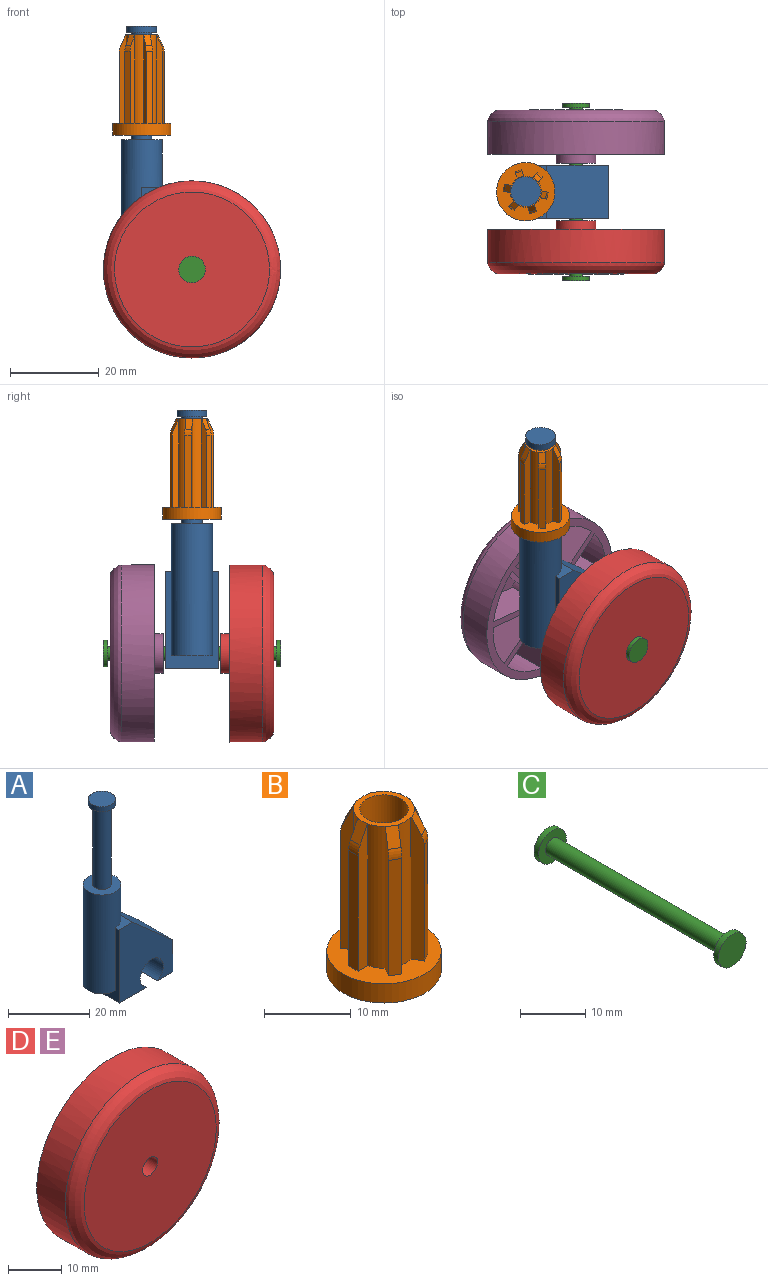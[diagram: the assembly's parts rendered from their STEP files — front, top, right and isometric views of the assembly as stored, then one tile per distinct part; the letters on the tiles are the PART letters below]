
ASSEMBLY  parts=5 mates=5
PART A: 16 faces, bbox 23.4x12x58.5 mm
  f0: plane 12x9.41mm, normal (0,0,-1), area 113mm2, adj f2,f5,f9,f10
  f1: plane 12x5.41mm, normal (0,0,-1), area 65mm2, adj f2,f8,f9,f10
  f2: plane 22x18.7mm, normal (0,-1,0), area 276.2mm2, adj f0,f1,f5,f6,f7,f8,f10
  f3: cylinder r=4.65mm len=29.8mm, axis (0,0,-1), area 593.1mm2, adj f4,f5,f7,f11
  f4: plane 9.3x4.65mm, normal (0,0,-1), area 34mm2, adj f3,f5
  f5: plane 22x12mm, normal (-1,0,0), area 87.3mm2, adj f0,f2,f3,f4,f7,f9
  f6: plane 14x12.32mm, normal (0.66,0,0.75), area 223.8mm2, adj f2,f7,f8,f9
  f7: plane 12x4.7mm, normal (0,0,1), area 22.4mm2, adj f2,f3,f5,f6,f9
  f8: plane 12x9.68mm, normal (1,0,0), area 116.1mm2, adj f1,f2,f6,f9
  f9: plane 22x18.7mm, normal (0,1,0), area 276.2mm2, adj f0,f1,f5,f6,f7,f8,f10
  f10: cylinder r=4mm len=12mm, axis (0,-1,0), area 253.1mm2, adj f0,f1,f2,f9
  f11: plane 9.3x9.3mm, normal (0,0,1), area 51.3mm2, adj f3,f15
  f12: plane 6.7x6.7mm, normal (0,0,1), area 35.3mm2, adj f13
  f13: cylinder r=3.35mm len=6.7mm, axis (0,0,-1), area 31.6mm2, adj f12,f14
  f14: plane 6.7x6.7mm, normal (0,0,-1), area 18.6mm2, adj f13,f15
  f15: cylinder r=2.3mm len=24.2mm, axis (0,0,-1), area 349.7mm2, adj f11,f14
PART B: 41 faces, bbox 13.2x13.2x22.7 mm
  f0: plane 13.2x13.2mm, normal (0,0,1), area 84.1mm2, adj f1,f2,f3,f4,f5,f7,f9,f11
  f1: cylinder r=3.5mm len=20mm, axis (0,0,1), area 42mm2, adj f0,f8,f27,f32
  f2: cylinder r=3.5mm len=20mm, axis (0,0,1), area 42mm2, adj f0,f8,f23,f28
  f3: cylinder r=3.5mm len=20mm, axis (0,0,1), area 42mm2, adj f0,f8,f19,f24
  f4: cylinder r=3.5mm len=20mm, axis (0,0,1), area 42mm2, adj f0,f8,f15,f20
  f5: cylinder r=3.5mm len=20mm, axis (0,0,1), area 42mm2, adj f0,f8,f11,f16
  f6: cylinder r=2.8mm len=22.7mm, axis (0,0,1), area 399.4mm2, adj f8,f10
  f7: cylinder r=3.5mm len=20mm, axis (0,0,1), area 42mm2, adj f0,f8,f12,f31
  f8: plane 7x7mm, normal (0,0,1), area 14.1mm2, adj f1,f2,f3,f4,f5,f6,f7,f11
  f9: cylinder r=6.6mm len=13.2mm, axis (0,0,1), area 112mm2, adj f0,f10
  f10: plane 13.2x13.2mm, normal (0,0,-1), area 112.2mm2, adj f6,f9
  f11: plane 20x1.59mm, normal (0,-1,0), area 29.4mm2, adj f0,f5,f8,f13,f14,f40
  f12: plane 20x1.59mm, normal (0,1,0), area 29.4mm2, adj f0,f7,f8,f13,f14,f40
  f13: plane 2.37x1.55mm, normal (0.89,0,0.45), area 4.1mm2, adj f8,f11,f12,f40
  f14: plane 16.29x1.55mm, normal (1,0,0), area 25.3mm2, adj f0,f11,f12,f40
  f15: plane 20x1.37mm, normal (-0.87,-0.5,0), area 29.4mm2, adj f0,f4,f8,f17,f18,f39
  f16: plane 20x1.37mm, normal (0.87,0.5,0), area 29.4mm2, adj f0,f5,f8,f17,f18,f39
  f17: plane 2.37x1.93mm, normal (0.45,-0.77,0.45), area 4.1mm2, adj f8,f15,f16,f39
  f18: plane 16.29x1.34mm, normal (0.5,-0.87,0), area 25.3mm2, adj f0,f15,f16,f39
  f19: plane 20x1.37mm, normal (-0.87,0.5,0), area 29.4mm2, adj f0,f3,f8,f21,f22,f38
  f20: plane 20x1.37mm, normal (0.87,-0.5,0), area 29.4mm2, adj f0,f4,f8,f21,f22,f38
  f21: plane 2.37x1.93mm, normal (-0.45,-0.77,0.45), area 4.1mm2, adj f8,f19,f20,f38
  f22: plane 16.29x1.34mm, normal (-0.5,-0.87,0), area 25.3mm2, adj f0,f19,f20,f38
  f23: plane 20x1.59mm, normal (0,1,0), area 29.4mm2, adj f0,f2,f8,f25,f26,f37
  f24: plane 20x1.59mm, normal (0,-1,0), area 29.4mm2, adj f0,f3,f8,f25,f26,f37
  f25: plane 2.37x1.55mm, normal (-0.89,0,0.45), area 4.1mm2, adj f8,f23,f24,f37
  f26: plane 16.29x1.55mm, normal (-1,0,0), area 25.3mm2, adj f0,f23,f24,f37
  f27: plane 20x1.37mm, normal (0.87,0.5,0), area 29.4mm2, adj f0,f1,f8,f29,f30,f36
  f28: plane 20x1.37mm, normal (-0.87,-0.5,0), area 29.4mm2, adj f0,f2,f8,f29,f30,f36
  f29: plane 2.37x1.93mm, normal (-0.45,0.77,0.45), area 4.1mm2, adj f8,f27,f28,f36
  f30: plane 16.29x1.34mm, normal (-0.5,0.87,0), area 25.3mm2, adj f0,f27,f28,f36
  f31: plane 20x1.37mm, normal (0.87,-0.5,0), area 29.4mm2, adj f0,f7,f8,f33,f34,f35
  f32: plane 20x1.37mm, normal (-0.87,0.5,0), area 29.4mm2, adj f0,f1,f8,f33,f34,f35
  f33: plane 2.37x1.93mm, normal (0.45,0.77,0.45), area 4.1mm2, adj f8,f31,f32,f35
  f34: plane 16.29x1.34mm, normal (0.5,0.87,0), area 25.3mm2, adj f0,f31,f32,f35
  f35: cylinder r=3mm len=1.5mm, axis (-0.87,0.5,0), area 2.2mm2, adj f31,f32,f33,f34
  f36: cylinder r=3mm len=1.5mm, axis (-0.87,-0.5,0), area 2.2mm2, adj f27,f28,f29,f30
  f37: cylinder r=3mm len=1.55mm, axis (0,-1,0), area 2.2mm2, adj f23,f24,f25,f26
  f38: cylinder r=3mm len=1.5mm, axis (0.87,-0.5,0), area 2.2mm2, adj f19,f20,f21,f22
  f39: cylinder r=3mm len=1.5mm, axis (0.87,0.5,0), area 2.2mm2, adj f15,f16,f17,f18
  f40: cylinder r=3mm len=1.55mm, axis (0,1,0), area 2.2mm2, adj f11,f12,f13,f14
PART C: 7 faces, bbox 6x40x6 mm
  f0: cylinder r=1.5mm len=38mm, axis (0,1,0), area 358.1mm2, adj f3,f6
  f1: cylinder r=3mm len=6mm, axis (0,-1,0), area 18.8mm2, adj f2,f3
  f2: plane 6x6mm, normal (0,1,0), area 28.3mm2, adj f1
  f3: plane 6x6mm, normal (0,-1,0), area 21.2mm2, adj f0,f1
  f4: cylinder r=3mm len=6mm, axis (0,1,0), area 18.8mm2, adj f5,f6
  f5: plane 6x6mm, normal (0,-1,0), area 28.3mm2, adj f4
  f6: plane 6x6mm, normal (0,1,0), area 21.2mm2, adj f0,f4
PART D: 55 faces, bbox 41x12x41 mm
  f0: cylinder r=4mm len=8mm, axis (0,1,0), area 13.1mm2, adj f1,f28,f39,f54
  f1: plane 14.68x11.44mm, normal (0,1,0), area 99.9mm2, adj f0,f2,f39,f54
  f2: cylinder r=18mm len=11.44mm, axis (0,-1,0), area 101.1mm2, adj f1,f35,f39,f54
  f3: plane 1.86x1.13mm, normal (0,-1,0), area 0.9mm2, adj f4,f30,f52,f53
  f4: cylinder r=4mm len=8mm, axis (0,1,0), area 13.1mm2, adj f3,f5,f52,f53
  f5: plane 14.68x11.44mm, normal (0,1,0), area 99.9mm2, adj f4,f6,f52,f53
  f6: cylinder r=18mm len=11.44mm, axis (0,-1,0), area 101.1mm2, adj f5,f35,f52,f53
  f7: plane 1.86x1.13mm, normal (0,-1,0), area 0.9mm2, adj f8,f30,f50,f51
  f8: cylinder r=4mm len=8mm, axis (0,1,0), area 13.1mm2, adj f7,f9,f50,f51
  f9: plane 14.68x11.44mm, normal (0,1,0), area 99.9mm2, adj f8,f10,f50,f51
  f10: cylinder r=18mm len=11.44mm, axis (0,-1,0), area 101.1mm2, adj f9,f35,f50,f51
  f11: plane 1.86x1.13mm, normal (0,-1,0), area 0.9mm2, adj f12,f30,f48,f49
  f12: cylinder r=4mm len=8mm, axis (0,1,0), area 13.1mm2, adj f11,f13,f48,f49
  f13: plane 14.68x11.44mm, normal (0,1,0), area 99.9mm2, adj f12,f14,f48,f49
  f14: cylinder r=18mm len=11.44mm, axis (0,-1,0), area 101.1mm2, adj f13,f35,f48,f49
  f15: plane 1.86x1.13mm, normal (0,-1,0), area 0.9mm2, adj f16,f30,f46,f47
  f16: cylinder r=4mm len=8mm, axis (0,1,0), area 13.1mm2, adj f15,f17,f46,f47
  f17: plane 14.68x11.44mm, normal (0,1,0), area 99.9mm2, adj f16,f18,f46,f47
  f18: cylinder r=18mm len=11.44mm, axis (0,-1,0), area 101.1mm2, adj f17,f35,f46,f47
  f19: plane 1.86x1.13mm, normal (0,-1,0), area 0.9mm2, adj f20,f30,f44,f45
  f20: cylinder r=4mm len=8mm, axis (0,1,0), area 13.1mm2, adj f19,f21,f44,f45
  f21: plane 14.68x11.44mm, normal (0,1,0), area 99.9mm2, adj f20,f22,f44,f45
  f22: cylinder r=18mm len=11.44mm, axis (0,-1,0), area 101.1mm2, adj f21,f35,f44,f45
  f23: plane 1.86x1.13mm, normal (0,-1,0), area 0.9mm2, adj f25,f30,f42,f43
  f24: plane 1.86x1.13mm, normal (0,-1,0), area 0.9mm2, adj f29,f30,f40,f41
  f25: cylinder r=4mm len=8mm, axis (0,1,0), area 13.1mm2, adj f23,f26,f42,f43
  f26: plane 14.68x11.44mm, normal (0,1,0), area 99.9mm2, adj f25,f27,f42,f43
  f27: cylinder r=18mm len=11.44mm, axis (0,-1,0), area 101.1mm2, adj f26,f35,f42,f43
  f28: plane 1.86x1.13mm, normal (0,-1,0), area 0.9mm2, adj f0,f30,f39,f54
  f29: cylinder r=4mm len=8mm, axis (0,1,0), area 13.1mm2, adj f24,f37,f40,f41
  f30: cylinder r=4.5mm len=9mm, axis (0,1,0), area 56.5mm2, adj f3,f7,f11,f15,f19,f23,f24,f28
  f31: plane 35.01x35.01mm, normal (0,-1,0), area 949.4mm2, adj f32,f36
  f32: cylinder r=2mm len=12mm, axis (0,1,0), area 150.8mm2, adj f31,f33
  f33: plane 9x9mm, normal (0,1,0), area 51.1mm2, adj f30,f32
  f34: cylinder r=20mm len=40mm, axis (0,-1,0), area 942.5mm2, adj f35,f36
  f35: plane 40x40mm, normal (0,1,0), area 400.9mm2, adj f2,f6,f10,f14,f18,f22,f27,f30
  f36: bspline ~41.04x41.04mm, area 451.9mm2, adj f31,f34
  f37: plane 14.68x11.44mm, normal (0,1,0), area 99.9mm2, adj f29,f38,f40,f41
  f38: cylinder r=18mm len=11.44mm, axis (0,-1,0), area 101.1mm2, adj f35,f37,f40,f41
  f39: plane 14.06x8mm, normal (1,0,0), area 112.4mm2, adj f0,f1,f2,f28,f35
  f40: plane 14.06x8mm, normal (-1,0,0), area 112.4mm2, adj f24,f29,f35,f37,f38
  f41: plane 9.94x9.94mm, normal (0.71,0,0.71), area 112.4mm2, adj f24,f29,f35,f37,f38
  f42: plane 9.94x9.94mm, normal (-0.71,0,-0.71), area 112.4mm2, adj f23,f25,f26,f27,f35
  f43: plane 14.06x8mm, normal (0,0,1), area 112.4mm2, adj f23,f25,f26,f27,f35
  f44: plane 14.06x8mm, normal (0,0,-1), area 112.4mm2, adj f19,f20,f21,f22,f35
  f45: plane 9.94x9.94mm, normal (-0.71,0,0.71), area 112.4mm2, adj f19,f20,f21,f22,f35
  f46: plane 9.94x9.94mm, normal (0.71,0,-0.71), area 112.4mm2, adj f15,f16,f17,f18,f35
  f47: plane 14.06x8mm, normal (-1,0,0), area 112.4mm2, adj f15,f16,f17,f18,f35
  f48: plane 14.06x8mm, normal (1,0,0), area 112.4mm2, adj f11,f12,f13,f14,f35
  f49: plane 9.94x9.94mm, normal (-0.71,0,-0.71), area 112.4mm2, adj f11,f12,f13,f14,f35
  f50: plane 9.94x9.94mm, normal (0.71,0,0.71), area 112.4mm2, adj f7,f8,f9,f10,f35
  f51: plane 14.06x8mm, normal (0,0,-1), area 112.4mm2, adj f7,f8,f9,f10,f35
  f52: plane 14.06x8mm, normal (0,0,1), area 112.4mm2, adj f3,f4,f5,f6,f35
  f53: plane 9.94x9.94mm, normal (0.71,0,-0.71), area 112.4mm2, adj f3,f4,f5,f6,f35
  f54: plane 9.94x9.94mm, normal (-0.71,0,0.71), area 112.4mm2, adj f0,f1,f2,f28,f35
PART E: same geometry as D
PLACE A at identity fixed
PLACE B rot(axis=(0,0,1),169.7deg) t=(0,0,0)mm
PLACE C rot(axis=(0,-1,0),170.6deg) t=(20.35,0,-28.67)mm
PLACE D rot(axis=(0,-1,0),8.4deg) t=(-1.86,0,-1.81)mm
PLACE E rot(axis=(0.9,0,-0.43),180deg) t=(-6.29,0,-13.22)mm
MATE revolute A.f10 <-> E.f0  axis (0,1,0) through (11.35,6,-13.5)mm
MATE pin_slot A.f10 <-> C.f0  axis (0,-1,0) through (11.35,0,-13.5)mm
MATE revolute C.f0 <-> A.f10  axis (0,1,0) through (11.35,0,-13.5)mm
MATE revolute B.f6 <-> A.f13  axis (0,0,1) through (0,0,39.5)mm
MATE revolute A.f10 <-> D.f0  axis (0,-1,0) through (11.35,-6,-13.5)mm
